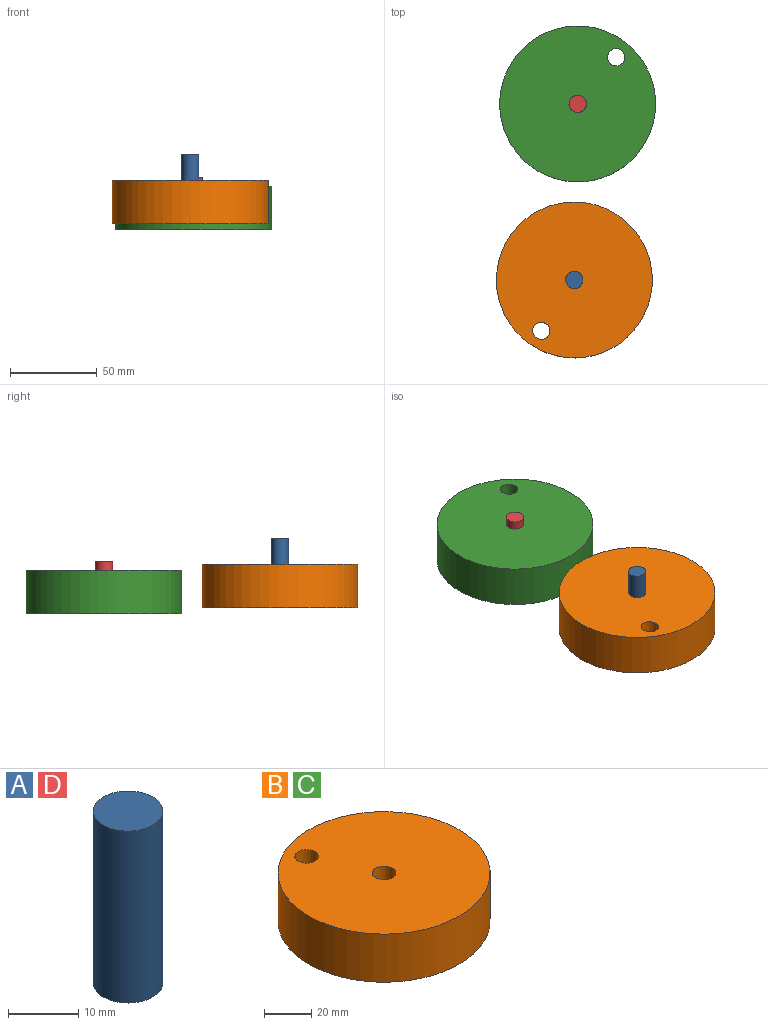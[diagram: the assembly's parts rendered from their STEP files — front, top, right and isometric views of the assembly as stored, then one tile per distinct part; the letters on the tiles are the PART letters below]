
ASSEMBLY  parts=4 mates=3
PART A: 3 faces, bbox 9.9x9.9x30 mm
  f0: cylinder r=4.96mm len=30mm, axis (0,0,-1), area 934.9mm2, adj f1,f2
  f1: plane 9.92x9.92mm, normal (0,0,1), area 77.3mm2, adj f0
  f2: plane 9.92x9.92mm, normal (0,0,-1), area 77.3mm2, adj f0
PART B: 5 faces, bbox 90x90x25 mm
  f0: cylinder r=45mm len=90mm, axis (0,0,-1), area 7068.6mm2, adj f1,f2
  f1: plane 90x90mm, normal (0,0,1), area 6204.6mm2, adj f0,f3,f4
  f2: plane 90x90mm, normal (0,0,-1), area 6204.6mm2, adj f0,f3,f4
  f3: cylinder r=5mm len=25mm, axis (0,0,1), area 785.4mm2, adj f1,f2
  f4: cylinder r=5mm len=25mm, axis (0,0,1), area 785.4mm2, adj f1,f2
PART C: same geometry as B
PART D: same geometry as A
PLACE A t=(-46.85,-58.27,-30)mm
PLACE B rot(axis=(0,0,1),122.4deg) t=(0,0,-40)mm
PLACE C rot(axis=(0,0,-1),64.2deg) t=(1.91,101.63,-43.43)mm
PLACE D rot(axis=(0,0,1),58.2deg) t=(26.79,31.12,-43.43)mm
MATE parallel B.f4 <-> C.f1  axis (0,0,1) through (-19.06,-29.37,-15)mm
MATE revolute D.f0 <-> C.f3  axis (0,0,-1) through (1.91,101.63,-43.43)mm
MATE revolute A.f0 <-> B.f3  axis (0,0,-1) through (0,0,-15)mm
